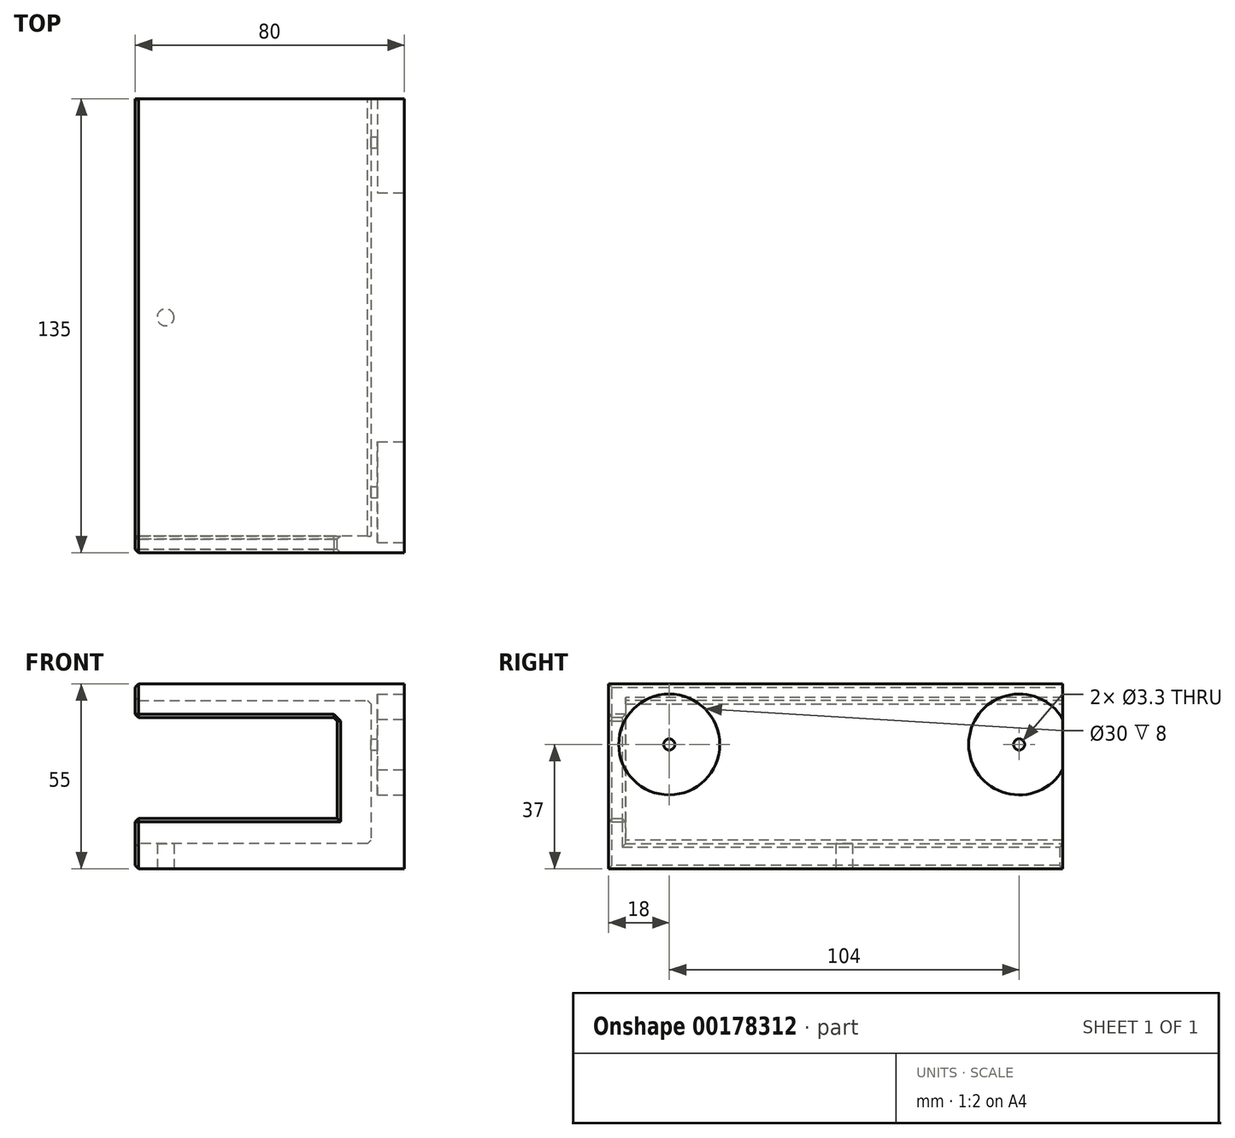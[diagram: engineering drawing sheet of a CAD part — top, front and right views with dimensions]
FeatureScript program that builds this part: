
annotation { "Feature Type Name" : "Feature", "Feature Type Description" : "" }
export const myFeature = defineFeature(function(context is Context, id is Id, definition is map)
    precondition{}
    {
        {
            var Q0;
            Q0=qCreatedBy(makeId("Front.planeOp"),FACE);
            var sketch = newSketch(context, id + "F0", { "sketchPlane" : qUnion([Q0])});
            skLineSegment(sketch, "E0", {"start": v(0, 0) * mm, "end": v(-80, 0) * mm});
            skLineSegment(sketch, "E1", {"start": v(-80, 0) * mm, "end": v(-80, -55) * mm});
            skLineSegment(sketch, "E2", {"start": v(-80, -55) * mm, "end": v(0, -55) * mm});
            skLineSegment(sketch, "E3", {"start": v(-80, -55) * mm, "end": v(-80, -40) * mm});
            skLineSegment(sketch, "E4", {"start": v(-80, 0) * mm, "end": v(-80, -10) * mm});
            skLineSegment(sketch, "E5", {"start": v(-80, -10) * mm, "end": v(-80, -40) * mm});
            skLineSegment(sketch, "E6", {"start": v(0, 0) * mm, "end": v(0, -55) * mm});
            skLineSegment(sketch, "E7", {"start": v(-80, -10) * mm, "end": v(-20, -10) * mm});
            skLineSegment(sketch, "E8", {"start": v(-80, -25) * mm, "end": v(-75.13, -25) * mm});
            skPoint(sketch, "E8.endSnap0", {"position": v(-80, -25) * mm});
            skLineSegment(sketch, "E9.MirrorCS", {"start": v(-80, -40) * mm, "end": v(-20, -40) * mm});
            skLineSegment(sketch, "E10", {"start": v(-20, -40) * mm, "end": v(-20, -10) * mm});
            skLineSegment(sketch, "E11", {"start": v(-80, 0) * mm, "end": v(-80, -5) * mm});
            skLineSegment(sketch, "E12", {"start": v(-80, -5) * mm, "end": v(-10, -5) * mm});
            skLineSegment(sketch, "E13", {"start": v(-10, -5) * mm, "end": v(-10, -47.5) * mm});
            skPoint(sketch, "E13.endSnap0", {"position": v(-80, -47.5) * mm});
            skLineSegment(sketch, "E14", {"start": v(-10, -47.5) * mm, "end": v(-80, -47.5) * mm});
            skSolve(sketch);
        }
        {
            var Q0;
            Q0=makeQuery(id+"F0.imprint","IMPRINT",FACE,{"disambiguationData":[TD([[makeQuery(id+"F0.imprint","IMPRINT",EDGE,{"derivedFrom":sQuery(id+"F0.wireOp",EDGE,"E0")}),1.0]])]});
            extrude(context, id + "F1", {"entities" : qUnion([Q0]), "depth" : 130 * mm});
        }
        {
            var Q0;
            Q0=makeQuery(id+"F0.imprint","IMPRINT",FACE,{"disambiguationData":[TD([[makeQuery(id+"F0.imprint","IMPRINT",EDGE,{"derivedFrom":sQuery(id+"F0.wireOp",EDGE,"E4")}),1.0]])]});
            var Q1;
            Q1=makeQuery(id+"F1.opExtrude","CAP_FACE",FACE,{"disambiguationData":[OSD([sQuery(id+"F0.wireOp",EDGE,"E0"),sQuery(id+"F0.wireOp",EDGE,"E2"),sQuery(id+"F0.wireOp",EDGE,"E3"),sQuery(id+"F0.wireOp",EDGE,"E6"),sQuery(id+"F0.wireOp",EDGE,"E11"),sQuery(id+"F0.wireOp",EDGE,"E12"),sQuery(id+"F0.wireOp",EDGE,"E13"),sQuery(id+"F0.wireOp",EDGE,"E14")])],"isStart":true});
            extrude(context, id + "F2", {"entities" : qUnion([Q0, Q1]), "operationType" : NewBodyOperationType.ADD, "oppositeDirection" : true, "depth" : 5 * mm});
        }
        {
            var Q0;
            Q0=makeQuery(id+"F1.opExtrude","CAP_FACE",FACE,{"disambiguationData":[OSD([sQuery(id+"F0.wireOp",EDGE,"E0"),sQuery(id+"F0.wireOp",EDGE,"E2"),sQuery(id+"F0.wireOp",EDGE,"E3"),sQuery(id+"F0.wireOp",EDGE,"E6"),sQuery(id+"F0.wireOp",EDGE,"E11"),sQuery(id+"F0.wireOp",EDGE,"E12"),sQuery(id+"F0.wireOp",EDGE,"E13"),sQuery(id+"F0.wireOp",EDGE,"E14")])],"isStart":false});
            var sketch = newSketch(context, id + "F3", { "sketchPlane" : qUnion([Q0])});
            skLineSegment(sketch, "E15", {"start": v(-80, -5) * mm, "end": v(-80, -10) * mm});
            skLineSegment(sketch, "E16", {"start": v(-80, -10) * mm, "end": v(-20, -10) * mm});
            skLineSegment(sketch, "E17", {"start": v(-20, -10) * mm, "end": v(-20, -40) * mm});
            skLineSegment(sketch, "E18", {"start": v(-20, -40) * mm, "end": v(-80, -40) * mm});
            skLineSegment(sketch, "E19", {"start": v(-80, -40) * mm, "end": v(-80, -55) * mm});
            skLineSegment(sketch, "E20", {"start": v(-80, -55) * mm, "end": v(0, -55) * mm});
            skLineSegment(sketch, "E21", {"start": v(0, -55) * mm, "end": v(0, 0) * mm});
            skLineSegment(sketch, "E22", {"start": v(0, 0) * mm, "end": v(-80, 0) * mm});
            skLineSegment(sketch, "E23", {"start": v(-80, 0) * mm, "end": v(-80, -10) * mm});
            skLineSegment(sketch, "E24", {"start": v(-80, -47.5) * mm, "end": v(-80, -40) * mm});
            skLineSegment(sketch, "E25", {"start": v(-80, -55) * mm, "end": v(-80, -47.5) * mm});
            skSolve(sketch);
        }
        {
            var Q0;
            {var subQ3=sQuery(id+"F3.wireOp",EDGE,"E16");Q0=makeQuery(id+"F3.imprint","IMPRINT",FACE,{"disambiguationData":[TD([[makeQuery(id+"F3.imprint","IMPRINT",EDGE,{"derivedFrom":subQ3}),1.0]])]});}
            var Q1;
            {var subQ2=sQuery(id+"F3.wireOp",EDGE,"E20");Q1=makeQuery(id+"F3.imprint","IMPRINT",FACE,{"disambiguationData":[TD([[makeQuery(id+"F3.imprint","IMPRINT",EDGE,{"derivedFrom":subQ2}),1.0]])]});}
            extrude(context, id + "F4", {"entities" : qUnion([Q0, Q1]), "operationType" : NewBodyOperationType.ADD, "depth" : 5 * mm});
        }
        {
            var Q0;
            Q0=makeQuery(id+"F4.opExtrude","CAP_EDGE",EDGE,{"disambiguationData":[OSD([sQuery(id+"F3.wireOp",EDGE,"E18")])],"isStart":false});
            var Q1;
            Q1=makeQuery(id+"F4.opExtrude","CAP_EDGE",EDGE,{"disambiguationData":[OSD([sQuery(id+"F3.wireOp",EDGE,"E17")])],"isStart":false});
            var Q2;
            Q2=makeQuery(id+"F4.opExtrude","CAP_EDGE",EDGE,{"disambiguationData":[OSD([sQuery(id+"F3.wireOp",EDGE,"E16")])],"isStart":false});
            var Q3;
            Q3=makeQuery(id+"F4.opExtrude","CAP_EDGE",EDGE,{"disambiguationData":[OSD([sQuery(id+"F3.wireOp",EDGE,"E18")])],"isStart":true});
            var Q4;
            Q4=makeQuery(id+"F4.opExtrude","CAP_EDGE",EDGE,{"disambiguationData":[OSD([sQuery(id+"F3.wireOp",EDGE,"E17")])],"isStart":true});
            var Q5;
            Q5=makeQuery(id+"F4.opExtrude","CAP_EDGE",EDGE,{"disambiguationData":[OSD([sQuery(id+"F3.wireOp",EDGE,"E16")])],"isStart":true});
            var Q6;
            Q6=makeQuery(id+"F2.opExtrude","CAP_EDGE",EDGE,{"disambiguationData":[OSD([sQuery(id+"F0.wireOp",EDGE,"E7")])],"isStart":true});
            var Q7;
            Q7=makeQuery(id+"F2.opExtrude","CAP_EDGE",EDGE,{"disambiguationData":[OSD([sQuery(id+"F0.wireOp",EDGE,"E7")])],"isStart":false});
            var Q8;
            Q8=makeQuery(id+"F2.opExtrude","CAP_EDGE",EDGE,{"disambiguationData":[OSD([sQuery(id+"F0.wireOp",EDGE,"E10")])],"isStart":true});
            var Q9;
            Q9=makeQuery(id+"F2.opExtrude","CAP_EDGE",EDGE,{"disambiguationData":[OSD([sQuery(id+"F0.wireOp",EDGE,"E10")])],"isStart":false});
            var Q10;
            Q10=makeQuery(id+"F2.opExtrude","CAP_EDGE",EDGE,{"disambiguationData":[OSD([sQuery(id+"F0.wireOp",EDGE,"E9.MirrorCS")])],"isStart":false});
            var Q11;
            Q11=makeQuery(id+"F2.opExtrude","SWEPT_EDGE",EDGE,{"disambiguationData":[OSD([sQuery(id+"F0.wireOp",EDGE,"E3"),sQuery(id+"F0.wireOp",EDGE,"E5"),sQuery(id+"F0.wireOp",EDGE,"E9.MirrorCS")])]});
            var Q12;
            Q12=makeQuery(id+"F2.opExtrude","CAP_EDGE",EDGE,{"disambiguationData":[OSD([sQuery(id+"F0.wireOp",EDGE,"E9.MirrorCS")])],"isStart":true});
            var Q13;
            Q13=makeQuery(id+"F2.opExtrude","SWEPT_EDGE",EDGE,{"disambiguationData":[OSD([sQuery(id+"F0.wireOp",EDGE,"E4"),sQuery(id+"F0.wireOp",EDGE,"E5"),sQuery(id+"F0.wireOp",EDGE,"E7")])]});
            var Q14;
            Q14=makeQuery(id+"F4.opExtrude","CAP_EDGE",EDGE,{"disambiguationData":[OSD([sQuery(id+"F3.wireOp",EDGE,"E19")])],"isStart":true});
            var Q15;
            Q15=makeQuery(id+"F1.opExtrude","SWEPT_EDGE",EDGE,{"disambiguationData":[OSD([sQuery(id+"F0.wireOp",EDGE,"E13"),sQuery(id+"F0.wireOp",EDGE,"E14")])]});
            var Q16;
            Q16=makeQuery(id+"F1.opExtrude","SWEPT_EDGE",EDGE,{"disambiguationData":[OSD([sQuery(id+"F0.wireOp",EDGE,"E4"),sQuery(id+"F0.wireOp",EDGE,"E11"),sQuery(id+"F0.wireOp",EDGE,"E12")])]});
            var Q17;
            Q17=makeQuery(id+"F2.boolean.opBoolean","MERGE",EDGE,{"derivedFrom":[makeQuery(id+"F2.opExtrude","CAP_EDGE",EDGE,{"disambiguationData":[OSD([sQuery(id+"F0.wireOp",EDGE,"E4")])],"isStart":true}),makeQuery(id+"F2.opExtrude","CAP_EDGE",EDGE,{"disambiguationData":[OSD([sQuery(id+"F0.wireOp",EDGE,"E11")])],"isStart":true})]});
            var Q18;
            Q18=makeQuery(id+"F1.opExtrude","SWEPT_EDGE",EDGE,{"disambiguationData":[OSD([sQuery(id+"F0.wireOp",EDGE,"E3"),sQuery(id+"F0.wireOp",EDGE,"E14")])]});
            var Q19;
            {var subQ0=sQuery(id+"F0.wireOp",EDGE,"E3");Q19=makeQuery(id+"F2.boolean.opBoolean","MERGE",EDGE,{"derivedFrom":[makeQuery(id+"F2.opExtrude","CAP_EDGE",EDGE,{"disambiguationData":[OSD([subQ0]),TDD([makeQuery(id+"F0.imprint","IMPRINT",EDGE,{"disambiguationData":[TD([[makeQuery(id+"F0.imprint","INTERSECT",VERTEX,{"derivedFrom":[subQ0,sQuery(id+"F0.wireOp",EDGE,"E14")]}),-1.0]])],"derivedFrom":subQ0})])],"isStart":true}),makeQuery(id+"F2.opExtrude","CAP_EDGE",EDGE,{"disambiguationData":[OSD([subQ0]),TDD([makeQuery(id+"F1.opExtrude","CAP_EDGE",EDGE,{"disambiguationData":[OSD([subQ0])],"isStart":true})])],"isStart":true})]});}
            var Q20;
            {var subQ0=sQuery(id+"F0.wireOp",EDGE,"E3");Q20=makeQuery(id+"F2.boolean.opBoolean","MERGE",EDGE,{"derivedFrom":[makeQuery(id+"F2.opExtrude","CAP_EDGE",EDGE,{"disambiguationData":[OSD([subQ0]),TDD([makeQuery(id+"F0.imprint","IMPRINT",EDGE,{"disambiguationData":[TD([[makeQuery(id+"F0.imprint","INTERSECT",VERTEX,{"derivedFrom":[subQ0,sQuery(id+"F0.wireOp",EDGE,"E14")]}),-1.0]])],"derivedFrom":subQ0})])],"isStart":false}),makeQuery(id+"F2.opExtrude","CAP_EDGE",EDGE,{"disambiguationData":[OSD([subQ0]),TDD([makeQuery(id+"F1.opExtrude","CAP_EDGE",EDGE,{"disambiguationData":[OSD([subQ0])],"isStart":true})])],"isStart":false})]});}
            var Q21;
            {var subQ0=sQuery(id+"F0.wireOp",EDGE,"E3");Q21=makeQuery(id+"F4.boolean.opBoolean","MERGE",FACE,{"derivedFrom":[makeQuery(id+"F2.boolean.opBoolean","MERGE",FACE,{"derivedFrom":[makeQuery(id+"F1.opExtrude","SWEPT_FACE",FACE,{"disambiguationData":[OSD([subQ0])]}),makeQuery(id+"F2.opExtrude","SWEPT_FACE",FACE,{"disambiguationData":[OSD([subQ0]),TDD([makeQuery(id+"F0.imprint","IMPRINT",EDGE,{"disambiguationData":[TD([[makeQuery(id+"F0.imprint","INTERSECT",VERTEX,{"derivedFrom":[subQ0,sQuery(id+"F0.wireOp",EDGE,"E14")]}),-1.0]])],"derivedFrom":subQ0})])]}),makeQuery(id+"F2.opExtrude","SWEPT_FACE",FACE,{"disambiguationData":[OSD([subQ0]),TDD([makeQuery(id+"F1.opExtrude","CAP_EDGE",EDGE,{"disambiguationData":[OSD([subQ0])],"isStart":true})])]})]}),makeQuery(id+"F4.opExtrude","SWEPT_FACE",FACE,{"disambiguationData":[OSD([sQuery(id+"F3.wireOp",EDGE,"E19")])]})]});}
            var Q22;
            Q22=makeQuery(id+"F4.opExtrude","SWEPT_EDGE",EDGE,{"disambiguationData":[OSD([sQuery(id+"F3.wireOp",EDGE,"E16"),sQuery(id+"F3.wireOp",EDGE,"E23")])]});
            var Q23;
            Q23=makeQuery(id+"F2.boolean.opBoolean","MERGE",EDGE,{"derivedFrom":[makeQuery(id+"F2.opExtrude","CAP_EDGE",EDGE,{"disambiguationData":[OSD([sQuery(id+"F0.wireOp",EDGE,"E4")])],"isStart":false}),makeQuery(id+"F2.opExtrude","CAP_EDGE",EDGE,{"disambiguationData":[OSD([sQuery(id+"F0.wireOp",EDGE,"E11")])],"isStart":false})]});
            var Q24;
            Q24=makeQuery(id+"F4.opExtrude","CAP_EDGE",EDGE,{"disambiguationData":[OSD([sQuery(id+"F3.wireOp",EDGE,"E23")])],"isStart":false});
            chamfer(context, id + "F5", {"entities" : qUnion([Q0, Q1, Q2, Q3, Q4, Q5, Q6, Q7, Q8, Q9, Q10, Q11, Q12, Q13, Q14, Q15, Q16, Q17, Q18, Q19, Q20, Q21, Q22, Q23, Q24]), "width" : 1 * mm, "tangentPropagation" : true});
        }
        {
            var Q0;
            {var subQ0=sQuery(id+"F0.wireOp",EDGE,"E6");Q0=makeQuery(id+"F4.boolean.opBoolean","MERGE",FACE,{"derivedFrom":[makeQuery(id+"F2.boolean.opBoolean","MERGE",FACE,{"derivedFrom":[makeQuery(id+"F1.opExtrude","SWEPT_FACE",FACE,{"disambiguationData":[OSD([subQ0])]}),makeQuery(id+"F2.opExtrude","SWEPT_FACE",FACE,{"disambiguationData":[OSD([subQ0])]})]}),makeQuery(id+"F4.opExtrude","SWEPT_FACE",FACE,{"disambiguationData":[OSD([sQuery(id+"F3.wireOp",EDGE,"E21")])]})]});}
            var sketch = newSketch(context, id + "F6", { "sketchPlane" : qUnion([Q0])});
            skLineSegment(sketch, "E26", {"start": v(-135, 0) * mm, "end": v(-135, -18) * mm});
            skLineSegment(sketch, "E27", {"start": v(-135, -18) * mm, "end": v(5, -18) * mm});
            skLineSegment(sketch, "E28", {"start": v(5, -18) * mm, "end": v(-13, -18) * mm});
            skLineSegment(sketch, "E29", {"start": v(-135, -18) * mm, "end": v(-117, -18) * mm});
            skCircle(sketch, "E30", {"center": v(-117, -18) * mm, "radius": 15 * mm});
            skCircle(sketch, "E31", {"center": v(-13, -18) * mm, "radius": 15 * mm});
            skCircle(sketch, "E32", {"center": v(-117, -18) * mm, "radius": 1.65 * mm});
            skCircle(sketch, "E33", {"center": v(-13, -18) * mm, "radius": 1.65 * mm});
            skSolve(sketch);
        }
        {
            var Q0;
            Q0 = qSketchRegion(id + "F6", true);
            extrude(context, id + "F7", {"entities" : qUnion([Q0]), "operationType" : NewBodyOperationType.REMOVE, "oppositeDirection" : true, "depth" : 8 * mm});
        }
        {
            var Q0;
            {var subQ0=sQuery(id+"F0.wireOp",EDGE,"E6");Q0=makeQuery(id+"F7.boolean.opBoolean","SPLIT",FACE,{"disambiguationData":[TD([makeQuery(id+"F7.opExtrude","SWEPT_FACE",FACE,{"disambiguationData":[OSD([sQuery(id+"F6.wireOp",EDGE,"E33")])]})])],"derivedFrom":makeQuery(id+"F4.boolean.opBoolean","MERGE",FACE,{"derivedFrom":[makeQuery(id+"F2.boolean.opBoolean","MERGE",FACE,{"derivedFrom":[makeQuery(id+"F1.opExtrude","SWEPT_FACE",FACE,{"disambiguationData":[OSD([subQ0])]}),makeQuery(id+"F2.opExtrude","SWEPT_FACE",FACE,{"disambiguationData":[OSD([subQ0])]})]}),makeQuery(id+"F4.opExtrude","SWEPT_FACE",FACE,{"disambiguationData":[OSD([sQuery(id+"F3.wireOp",EDGE,"E21")])]})]})});}
            var Q1;
            {var subQ0=sQuery(id+"F0.wireOp",EDGE,"E6");Q1=makeQuery(id+"F7.boolean.opBoolean","SPLIT",FACE,{"disambiguationData":[TD([makeQuery(id+"F7.opExtrude","SWEPT_FACE",FACE,{"disambiguationData":[OSD([sQuery(id+"F6.wireOp",EDGE,"E32")])]})])],"derivedFrom":makeQuery(id+"F4.boolean.opBoolean","MERGE",FACE,{"derivedFrom":[makeQuery(id+"F2.boolean.opBoolean","MERGE",FACE,{"derivedFrom":[makeQuery(id+"F1.opExtrude","SWEPT_FACE",FACE,{"disambiguationData":[OSD([subQ0])]}),makeQuery(id+"F2.opExtrude","SWEPT_FACE",FACE,{"disambiguationData":[OSD([subQ0])]})]}),makeQuery(id+"F4.opExtrude","SWEPT_FACE",FACE,{"disambiguationData":[OSD([sQuery(id+"F3.wireOp",EDGE,"E21")])]})]})});}
            var Q2;
            Q2=sQuery(id+"F6.wireOp",EDGE,"E33");
            extrude(context, id + "F8", {"entities" : qUnion([Q0, Q1]), "operationType" : NewBodyOperationType.REMOVE, "surfaceEntities" : qUnion([Q2]), "oppositeDirection" : true, "depth" : 20 * mm});
        }
        {
            var Q0;
            {var subQ0=sQuery(id+"F0.wireOp",EDGE,"E2");Q0=makeQuery(id+"F4.boolean.opBoolean","MERGE",FACE,{"derivedFrom":[makeQuery(id+"F2.boolean.opBoolean","MERGE",FACE,{"derivedFrom":[makeQuery(id+"F1.opExtrude","SWEPT_FACE",FACE,{"disambiguationData":[OSD([subQ0])]}),makeQuery(id+"F2.opExtrude","SWEPT_FACE",FACE,{"disambiguationData":[OSD([subQ0])]})]}),makeQuery(id+"F4.opExtrude","SWEPT_FACE",FACE,{"disambiguationData":[OSD([sQuery(id+"F3.wireOp",EDGE,"E20")])]})]});}
            var sketch = newSketch(context, id + "F9", { "sketchPlane" : qUnion([Q0])});
            skLineSegment(sketch, "E34", {"start": v(-79, 65) * mm, "end": v(-71, 65) * mm});
            skCircle(sketch, "E35", {"center": v(-71, 65) * mm, "radius": 2.5 * mm});
            skSolve(sketch);
        }
        {
            var Q0;
            Q0 = qSketchRegion(id + "F9", true);
            extrude(context, id + "F10", {"entities" : qUnion([Q0]), "operationType" : NewBodyOperationType.REMOVE, "oppositeDirection" : true, "depth" : 10 * mm});
        }
    });
